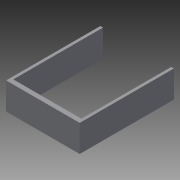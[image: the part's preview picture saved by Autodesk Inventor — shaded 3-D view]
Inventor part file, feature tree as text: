
AUTODESK INVENTOR PART (.ipt)
format: ipt  version: 2013 (Build 170138000, 138)  size: 82,432 bytes
history: native  units: mm
features: extrude x2, sketch x2, other x1
ambient origin geometry x8: Origin, YZ Plane, XZ Plane, XY Plane, X Axis, Y Axis, Z Axis, Center Point
feature tree (5):
  other  "ソリッド1"
  extrude  "押し出し1"  Depth=82.0mm
  extrude  "押し出し2"  Depth=30.0mm
  sketch  "スケッチ1"
  sketch  "スケッチ2"
